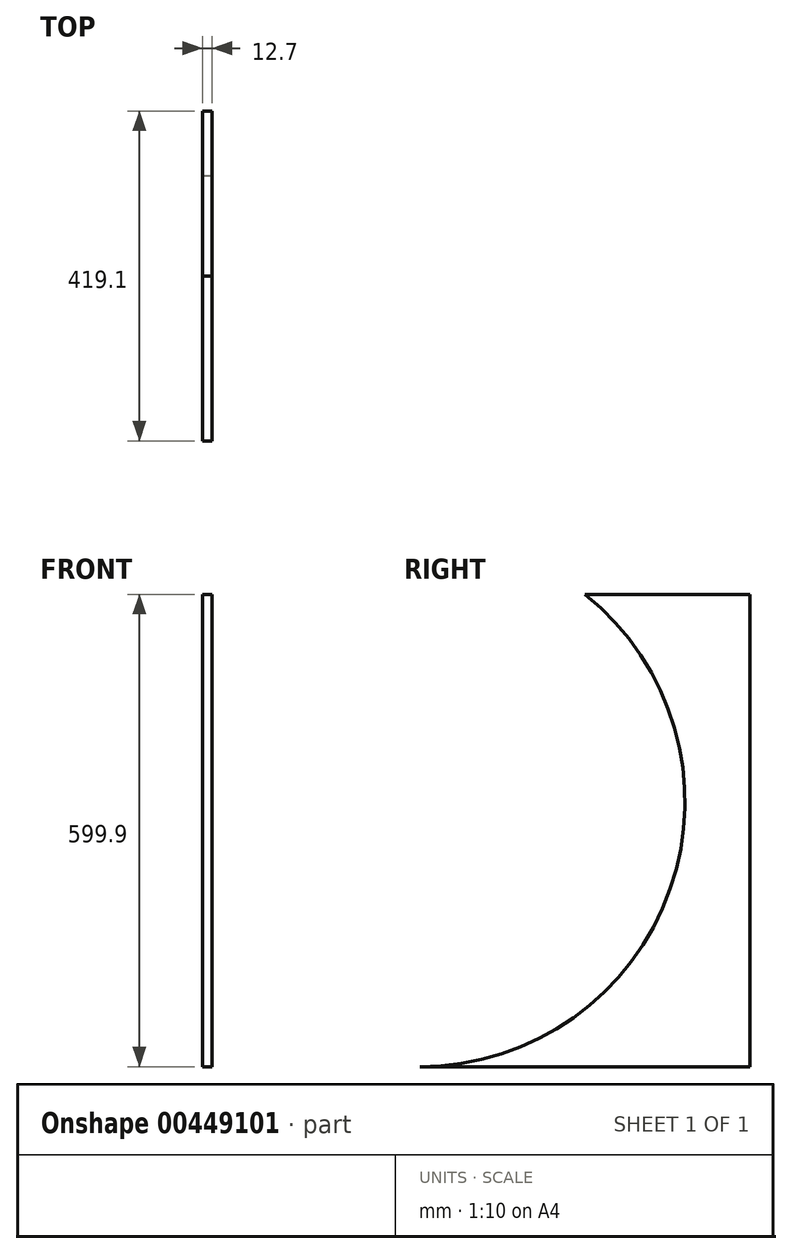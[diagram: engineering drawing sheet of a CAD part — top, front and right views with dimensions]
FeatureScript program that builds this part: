
annotation { "Feature Type Name" : "Feature", "Feature Type Description" : "" }
export const myFeature = defineFeature(function(context is Context, id is Id, definition is map)
    precondition{}
    {
        {
            var Q0;
            Q0=qCreatedBy(makeId("Right.planeOp"),FACE);
            var sketch = newSketch(context, id + "F0", { "sketchPlane" : qUnion([Q0])});
            skLineSegment(sketch, "E0.top", {"start": v(209.55, -209.55) * mm, "end": v(-209.55, -209.55) * mm});
            skLineSegment(sketch, "E0.left", {"start": v(209.55, 209.55) * mm, "end": v(209.55, -209.55) * mm});
            skPoint(sketch, "E0.middle", {"position": v(0, 0) * mm});
            skPoint(sketch, "E1.orphan", {"position": v(-209.55, 209.55) * mm});
            skLineSegment(sketch, "E2", {"start": v(209.55, 209.55) * mm, "end": v(209.55, 390.35) * mm});
            skArc(sketch, "E3", {"start": v(-209.55, -209.55) * mm, "mid": v(108.17, 16.02) * mm, "end": v(0, 390.35) * mm});
            skLineSegment(sketch, "E4", {"start": v(0, 390.35) * mm, "end": v(209.55, 390.35) * mm});
            skSolve(sketch);
        }
        {
            var Q0;
            Q0 = qSketchRegion(id + "F0", true);
            extrude(context, id + "F1", {"entities" : qUnion([Q0]), "depth" : 12.7 * mm});
        }
    });
